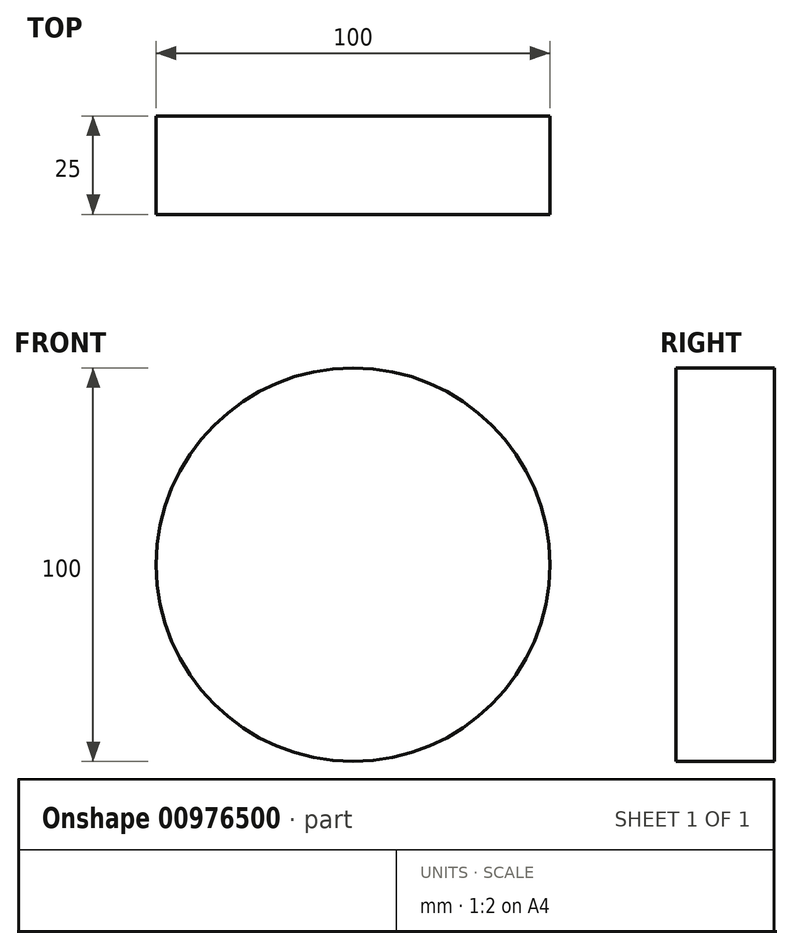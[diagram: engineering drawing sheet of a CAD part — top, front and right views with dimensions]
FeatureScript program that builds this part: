
annotation { "Feature Type Name" : "Feature", "Feature Type Description" : "" }
export const myFeature = defineFeature(function(context is Context, id is Id, definition is map)
    precondition{}
    {
        {
            var Q0;
            Q0=qCreatedBy(makeId("Front.planeOp"),FACE);
            var sketch = newSketch(context, id + "F0", { "sketchPlane" : qUnion([Q0])});
            skLineSegment(sketch, "E0", {"start": v(17.62, 46.8) * mm, "end": v(17.62, 46.8) * mm});
            skArc(sketch, "E1", {"start": v(49.46, -7.35) * mm, "mid": v(43.1, 25.35) * mm, "end": v(17.62, 46.8) * mm});
            skArc(sketch, "E2", {"start": v(17.62, 46.8) * mm, "mid": v(-43.1, -25.35) * mm, "end": v(49.46, -7.35) * mm});
            skSolve(sketch);
        }
        {
            var Q0;
            Q0 = qSketchRegion(id + "F0", true);
            extrude(context, id + "F1", {"entities" : qUnion([Q0]), "depth" : 25 * mm, "offsetDistance" : 25 * mm});
        }
    });
